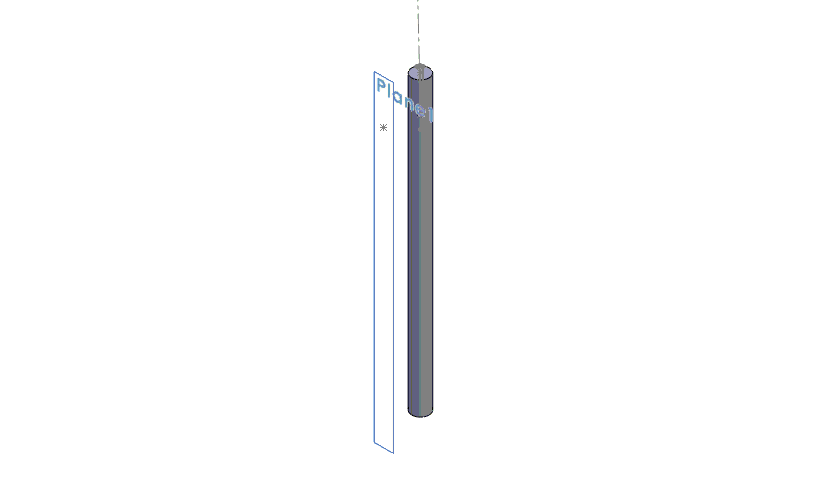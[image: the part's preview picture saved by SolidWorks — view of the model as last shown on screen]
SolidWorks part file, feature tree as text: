
SOLIDWORKS PART (.sldprt)
format: sldprt  version: not decoded by parser v0  size: 126,976 bytes
history: native  units: mm
features: sketch x5, material x1, extrude x1, plane x1, hole x1 (+12 scaffold rows collapsed)
feature tree (21):
  scaffold x12  (default folders/planes/origin — collapsed)
  material  "Material <not specified>"
  sketch  "Sketch1"  dims[D1=3.0mm]
  extrude  "Boss-Extrude1"  Depth=100mm
  sketch  "Sketch2"
  plane  "Plane1"  Offset=12.54mm
  sketch  "Sketch3"  dims[D1=10.0mm]
  hole  "Ø1.5mm Dowel Hole5"  Diameter=1.5mm Depth=20mm
  sketch  "3DSketch4"  dims[D1=~10.611629mm]
  sketch  "Sketch7"  dims[hole-wizard template sketch: 47 standard entries collapsed; hole parameters kept: c15.Hole Depth=20.0mm c15.D3=~14.816244mm c15.Drill Angle=118.0deg]
decode coverage: 6 of 7 modeling features carry decoded parameters
note: ~ marks probable driven/reference dimensions
note: suppression state not decoded; provenance and decode notes live in map.json
